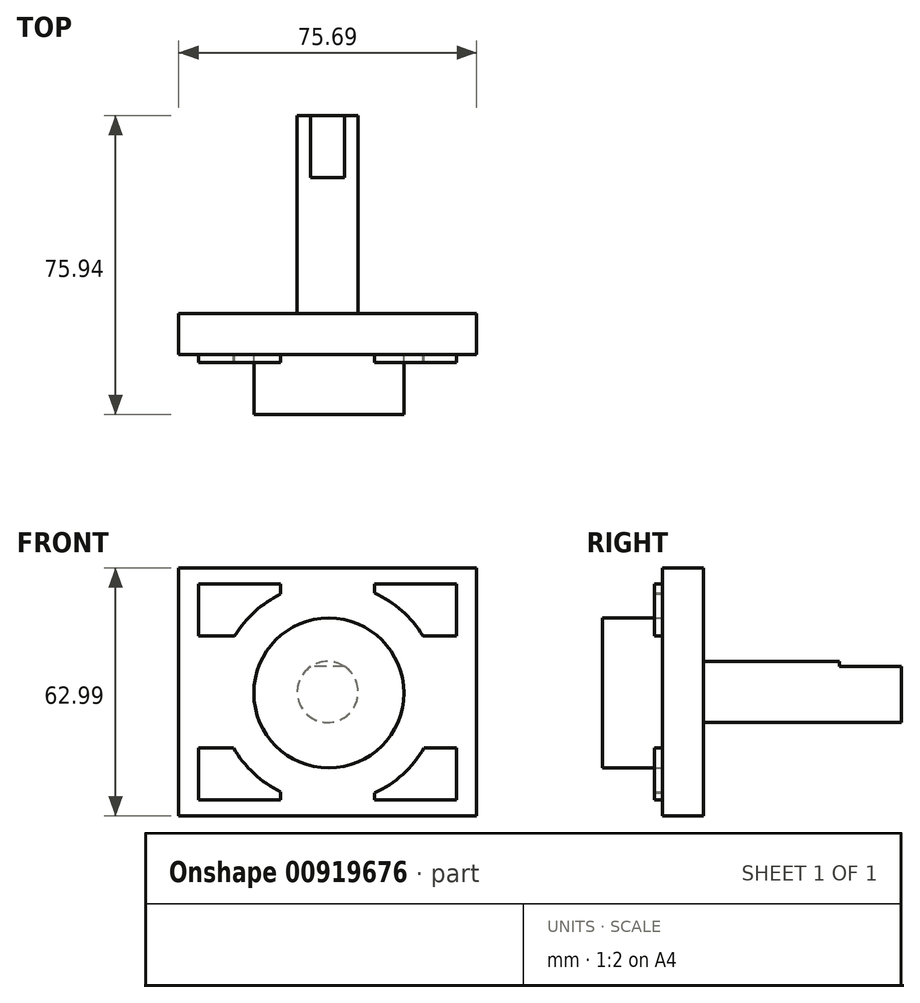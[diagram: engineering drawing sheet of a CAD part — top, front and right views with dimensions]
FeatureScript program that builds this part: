
annotation { "Feature Type Name" : "Feature", "Feature Type Description" : "" }
export const myFeature = defineFeature(function(context is Context, id is Id, definition is map)
    precondition{}
    {
        {
            var Q0;
            Q0=qCreatedBy(makeId("Front.planeOp"),FACE);
            var sketch = newSketch(context, id + "F0", { "sketchPlane" : qUnion([Q0])});
            skLineSegment(sketch, "E0.bottom", {"start": v(0, 0) * mm, "end": v(75.7, 0) * mm});
            skLineSegment(sketch, "E0.top", {"start": v(0, 63) * mm, "end": v(75.7, 63) * mm});
            skLineSegment(sketch, "E0.left", {"start": v(0, 0) * mm, "end": v(0, 63) * mm});
            skLineSegment(sketch, "E0.right", {"start": v(75.7, 0) * mm, "end": v(75.7, 63) * mm});
            skSolve(sketch);
        }
        {
            var Q0;
            Q0 = qSketchRegion(id + "F0", true);
            extrude(context, id + "F1", {"entities" : qUnion([Q0]), "depth" : 10.4 * mm, "offsetDistance" : 25.4 * mm});
        }
        {
            var Q0;
            Q0=makeQuery(id+"F1.opExtrude","CAP_FACE",FACE,{"disambiguationData":[OSD([sQuery(id+"F0.wireOp",EDGE,"E0.bottom"),sQuery(id+"F0.wireOp",EDGE,"E0.top"),sQuery(id+"F0.wireOp",EDGE,"E0.left"),sQuery(id+"F0.wireOp",EDGE,"E0.right")])],"isStart":false});
            var sketch = newSketch(context, id + "F2", { "sketchPlane" : qUnion([Q0])});
            skLineSegment(sketch, "E1.bottom", {"start": v(5.08, 4.06) * mm, "end": v(25.9, 4.06) * mm});
            skLineSegment(sketch, "E1.top", {"start": v(5.08, 58.93) * mm, "end": v(25.9, 58.93) * mm});
            skLineSegment(sketch, "E1.left", {"start": v(5.08, 4.06) * mm, "end": v(5.08, 17.27) * mm});
            skLineSegment(sketch, "E1.right", {"start": v(70.61, 4.06) * mm, "end": v(70.61, 17.27) * mm});
            skArc(sketch, "E2", {"start": v(49.78, 5.83) * mm, "mid": v(56.95, 10.57) * mm, "end": v(62.34, 17.27) * mm});
            skArc(sketch, "E3.trimOffspring", {"start": v(25.9, 56.35) * mm, "mid": v(19.31, 51.88) * mm, "end": v(14.25, 45.72) * mm});
            skLineSegment(sketch, "E4", {"start": v(25.9, 58.93) * mm, "end": v(25.9, 56.35) * mm});
            skLineSegment(sketch, "E5", {"start": v(25.9, 6.1) * mm, "end": v(25.9, 4.06) * mm});
            skLineSegment(sketch, "E6.trimOffspring", {"start": v(49.78, 58.93) * mm, "end": v(70.61, 58.93) * mm});
            skLineSegment(sketch, "E7.trimOffspring", {"start": v(49.78, 4.06) * mm, "end": v(70.61, 4.06) * mm});
            skLineSegment(sketch, "E8", {"start": v(5.08, 45.72) * mm, "end": v(14.25, 45.72) * mm});
            skLineSegment(sketch, "E9", {"start": v(5.08, 17.27) * mm, "end": v(13.93, 17.27) * mm});
            skArc(sketch, "E10.trimOffspring", {"start": v(13.93, 17.27) * mm, "mid": v(19.08, 10.8) * mm, "end": v(25.9, 6.1) * mm});
            skLineSegment(sketch, "E11.trimOffspring", {"start": v(5.08, 45.72) * mm, "end": v(5.08, 58.93) * mm});
            skLineSegment(sketch, "E12", {"start": v(49.78, 5.83) * mm, "end": v(49.78, 4.06) * mm});
            skLineSegment(sketch, "E13", {"start": v(62.02, 45.72) * mm, "end": v(70.61, 45.72) * mm});
            skLineSegment(sketch, "E14", {"start": v(62.34, 17.27) * mm, "end": v(70.61, 17.27) * mm});
            skPoint(sketch, "E15.orphan", {"position": v(34.49, 58.93) * mm});
            skPoint(sketch, "E16.start.orphan", {"position": v(52.55, 58.93) * mm});
            skLineSegment(sketch, "E17", {"start": v(49.78, 58.93) * mm, "end": v(49.78, 56.62) * mm});
            skArc(sketch, "E18.trimOffspring", {"start": v(62.02, 45.72) * mm, "mid": v(56.72, 52.09) * mm, "end": v(49.78, 56.62) * mm});
            skLineSegment(sketch, "E19.trimOffspring", {"start": v(70.61, 45.72) * mm, "end": v(70.61, 58.93) * mm});
            skSolve(sketch);
        }
        {
            var Q0;
            {var subQ0=sQuery(id+"F2.wireOp",EDGE,"E1.right");Q0=makeQuery(id+"F2.imprint","IMPRINT",FACE,{"disambiguationData":[TD([[makeQuery(id+"F2.imprint","IMPRINT",EDGE,{"derivedFrom":subQ0}),1.0]])]});}
            var Q1;
            {var subQ0=sQuery(id+"F2.wireOp",EDGE,"E1.left");Q1=makeQuery(id+"F2.imprint","IMPRINT",FACE,{"disambiguationData":[TD([[makeQuery(id+"F2.imprint","IMPRINT",EDGE,{"derivedFrom":subQ0}),-1.0]])]});}
            var Q2;
            Q2=makeQuery(id+"F2.imprint","IMPRINT",FACE,{"disambiguationData":[TD([[makeQuery(id+"F2.imprint","IMPRINT",EDGE,{"derivedFrom":sQuery(id+"F2.wireOp",EDGE,"E1.top")}),-1.0]])]});
            var Q3;
            Q3=makeQuery(id+"F2.imprint","IMPRINT",FACE,{"disambiguationData":[TD([[makeQuery(id+"F2.imprint","IMPRINT",EDGE,{"derivedFrom":sQuery(id+"F2.wireOp",EDGE,"E6.trimOffspring")}),-1.0]])]});
            extrude(context, id + "F3", {"entities" : qUnion([Q0, Q1, Q2, Q3]), "operationType" : NewBodyOperationType.ADD, "depth" : 2.03 * mm, "offsetDistance" : 25.4 * mm});
        }
        {
            var Q0;
            Q0=makeQuery(id+"F1.opExtrude","CAP_FACE",FACE,{"disambiguationData":[OSD([sQuery(id+"F0.wireOp",EDGE,"E0.bottom"),sQuery(id+"F0.wireOp",EDGE,"E0.top"),sQuery(id+"F0.wireOp",EDGE,"E0.left"),sQuery(id+"F0.wireOp",EDGE,"E0.right")])],"isStart":false});
            var sketch = newSketch(context, id + "F4", { "sketchPlane" : qUnion([Q0])});
            skCircle(sketch, "E20", {"center": v(38.13, 31.23) * mm, "radius": 19.05 * mm});
            skSolve(sketch);
        }
        {
            var Q0;
            Q0=makeQuery(id+"F4.imprint","IMPRINT",FACE,{"disambiguationData":[TD([[makeQuery(id+"F4.imprint","IMPRINT",EDGE,{"derivedFrom":sQuery(id+"F4.wireOp",EDGE,"E20")}),1.0]])]});
            extrude(context, id + "F5", {"entities" : qUnion([Q0]), "operationType" : NewBodyOperationType.ADD, "depth" : 15.24 * mm, "offsetDistance" : 25.4 * mm});
        }
        {
            var Q0;
            Q0=makeQuery(id+"F1.opExtrude","CAP_FACE",FACE,{"disambiguationData":[OSD([sQuery(id+"F0.wireOp",EDGE,"E0.bottom"),sQuery(id+"F0.wireOp",EDGE,"E0.top"),sQuery(id+"F0.wireOp",EDGE,"E0.left"),sQuery(id+"F0.wireOp",EDGE,"E0.right")])],"isStart":true});
            var sketch = newSketch(context, id + "F6", { "sketchPlane" : qUnion([Q0])});
            skLineSegment(sketch, "E21.0", {"start": v(-75.7, 0) * mm, "end": v(-75.7, 63) * mm});
            skLineSegment(sketch, "E22.0.0", {"start": v(0, 63) * mm, "end": v(-75.7, 63) * mm});
            skLineSegment(sketch, "E22.0.1", {"start": v(-75.7, 63) * mm, "end": v(-75.7, 0) * mm});
            skLineSegment(sketch, "E22.0.2", {"start": v(-75.7, 0) * mm, "end": v(0, 0) * mm});
            skLineSegment(sketch, "E22.0.3", {"start": v(0, 0) * mm, "end": v(0, 63) * mm});
            skLineSegment(sketch, "E23", {"start": v(-37.85, 71.82) * mm, "end": v(-37.85, -14.71) * mm, "construction": true});
            skPoint(sketch, "E23.startSnap0", {"position": v(-37.85, 63) * mm});
            skPoint(sketch, "E23.endSnap0", {"position": v(-37.85, 0) * mm});
            skLineSegment(sketch, "E24", {"start": v(-82.31, 31.5) * mm, "end": v(22.47, 31.5) * mm, "construction": true});
            skPoint(sketch, "E24.startSnap0", {"position": v(-75.7, 31.5) * mm});
            skCircle(sketch, "E25", {"center": v(-37.85, 31.5) * mm, "radius": 7.75 * mm});
            skLineSegment(sketch, "E26", {"start": v(-42.16, 37.93) * mm, "end": v(-33.53, 37.93) * mm});
            skSolve(sketch);
        }
        {
            var Q0;
            {var subQ0=sQuery(id+"F6.wireOp",EDGE,"E26");Q0=makeQuery(id+"F6.imprint","IMPRINT",FACE,{"disambiguationData":[TD([[makeQuery(id+"F6.imprint","IMPRINT",EDGE,{"derivedFrom":subQ0}),-1.0]])]});}
            extrude(context, id + "F7", {"entities" : qUnion([Q0]), "operationType" : NewBodyOperationType.ADD, "depth" : 50.3 * mm, "offsetDistance" : 25.4 * mm});
        }
        {
            var Q0;
            {var subQ0=sQuery(id+"F6.wireOp",EDGE,"E26");Q0=makeQuery(id+"F6.imprint","IMPRINT",FACE,{"disambiguationData":[TD([[makeQuery(id+"F6.imprint","IMPRINT",EDGE,{"derivedFrom":subQ0}),1.0]])]});}
            extrude(context, id + "F8", {"entities" : qUnion([Q0]), "operationType" : NewBodyOperationType.ADD, "depth" : 34.54 * mm, "offsetDistance" : 25.4 * mm});
        }
    });
